# Revit family: bremerhaven_led_vht_m1200__pc_tropal_r__bruchsicher__4000k_breitstrahlend_5974804484_5f1f
name_source: partatom
category: Lighting Fixtures
units: mm (PartAtom-declared; Revit-internal decimal feet)

## family parameters
Cut with Voids When Loaded = No
Host = Face
Light Source = No
Part Type = Normal
Room Calculation Point = No
Round Connector Dimension = Use Diameter
Shared = No

## types (1)
- BREMERHAVEN LED VHT m1200, PC Tropal® bruchsicher, 4000K breitstrahlend (1 x LED Stripe, 3640 lm, 23 W, 840/4000K)
    Apparent Load = 26 VA
    Approval mark = CE, ENEC
    CIE Flux Codes = 46 77 93 94 96
    Color Rendering = 1B/80..89
    Color Temperature = 840/4000K
    Default Elevation = 1800 mm
    Description = Polymer luminaire with LED lamps. Useable in industrial applications with demanding ambient conditions. Suitable for production facilities and suppliers in the food and beverages industry. Heat-resistant (high temperature (HT)) version suitable for temperatures up to +60 °C, highly heat-resistant (very high-temperature (VHT)) version suitable for temperatures up to +90 °C. Weatherproof luminaire housing made of thermosetting polymer. Useable for indoor and outdoor areas according to protection rating IP 65, IP 66, IP 67 and IP 68, 1 m. Thermally separated lamp chamber and driver chamber. Short sealing system consisting of age-resistant, form-retaining silicone/synthetic rubber. Protection tube 38 mm made of PC Tropal® (fracture proof). Luminaire ready for mounting and installation. Two M20 cable glands on face side. Single or row mounting (HT version only). Ceiling installation using two polymer stirrup clamps, variable mounting distance.


Length: 1432 mm
Width: 77 mm
Height: 129 mm
Weight: 2.7 kg

LOR: 95.5 %
    Height = 129 mm
    Lamp = 1 x LED Stripe
    Lamp Light Flux = 3640 lm
    Lamp Power = 23 W
    Lamp count = 1
    Length = 1432 mm
    Lifetime = 50000 h
    Luminous efficacy = 134 lm/W
    Manufacturer = NORKA
    ModVariant = No
    Model = 5974804484
    Mounting Place = Ceiling, Wall
    Mounting Type = Pendant, Surface mounted
    Number of Poles = 1
    OnlyDefault = Yes
    Power Factor = 1
    Product Name = BREMERHAVEN LED VHT m1200, PC Tropal® bruchsicher, 4000K breitstrahlend
    Product group = Ceiling-/wall luminaire
    ProductGroupID = 30
    Protection Class = Protection class II
    Protection Degree = IP 66
    RLX_Detail_Level = 1
    RlxData = <blob elided: 149505 chars, md5=5340f8db>
    Socket = socket
    Standby Power = 0 W
    System Light Flux = 3476 lm
    System Power = 26 W
    Type Comments = Product without accessories
    Type Image = bremerhaven_led_web.jpg
    URL = http://relux.com
    VarID = ---
    Voltage = 0 V
    Weight = 0.00 kg
    Width = 77 mm

## geometry (parser evidence)
native form markers: Sweep x13
no freeform markers — native parametric forms only
